# Revit family: QF_Kienle_PK600B
name_source: partatom
category: Sonderausstattung
units: mm (PartAtom-declared; Revit-internal decimal feet)

## family parameters
Arbeitsebenenbasiert = Nein
Beim Laden mit Abzugskörper schneiden = Nein
Bemaßung runder Anschluss = Durchmesser verwenden
Beschriftungsausrichtung beibehalten = Nein
Gemeinsam genutzt = Nein
Immer vertikal = Ja
OmniClass-Nummer = 23.40.40.14.17
OmniClass-Titel = Food Cooking Equipment
Raumberechnungspunkt = Nein
Schneiden in Ansichten zulassen = Nein
Teiletyp = Normal

## types (1)
- 3NAC - 400 V - 50 Hz
    Abwassertemperatur = 100 °C
    Anzahl der Pole = 3
    Beschreibung = Pastakocher (1 Becken à 45 Liter - GN 1/1), Standmodell
    CE Kennzeichnung = Ja
    Fehlstromschutzschalter Typ = A
    Frequenz = 50 Hz
    Gewicht = 86.00 kg
    Hersteller = Kienle
    IP Schutzart = 65
    Indirekte Ablaufanschlussgröße = 25 mm
    Indirekter Abwasserstrom = 0.7 L/s
    Kaltwasser Durchflussmenge = 0.1 L/s
    Kaltwasseranschlussgröße = 19 mm
    Kaltwasserdruck Maximum = 600000.0 Pa
    Kaltwasserdruck Minimum = 200000.0 Pa
    Kaltwasserqualität = 3-5°dH
    Kaltwassertemperatur empfohlen = 30 °C
    Kosten = 0 $
    Latente Abwärme Belastung = 3100 W
    Länge Gerätebreite = 604 mm
    Modell = PK600B
    Phasen = 3
    Restfeuchte der Abluft = 4600
    Sensible Abwärme Belastung = 1900 W
    Spannung = 400 V
    Stecker System = CEE 32
    Tiefe = 680 mm
    URL = https://www.kienle-fritteusen.de
    Vorgabe-Ansicht = 0 mm  [stored 0 ft]
    Warnhinweise = W017 / W012 (ISO 7010)
    Watt Leistung = 15600 W

note: [stored X ft] marks values corroborated as IEEE doubles in the binary element streams (Revit-internal decimal feet)
